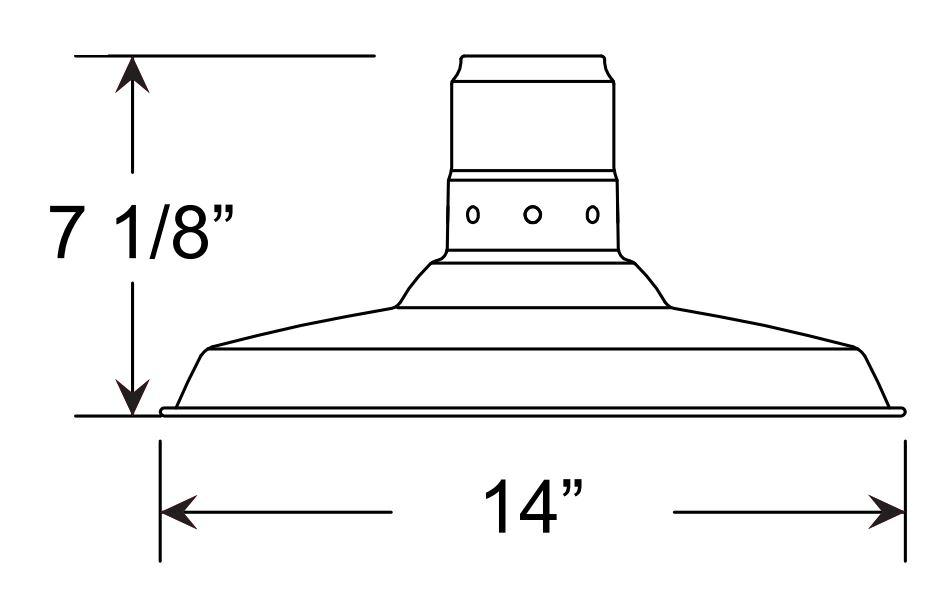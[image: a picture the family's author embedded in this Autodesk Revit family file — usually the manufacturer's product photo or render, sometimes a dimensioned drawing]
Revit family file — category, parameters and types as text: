
# Revit family: Shallow Dome_LED
name_source: partatom
category: Lighting Fixtures
units: mm (PartAtom-declared; Revit-internal decimal feet)

## family parameters
Always vertical = Yes
Cut with Voids When Loaded = No
Light Source = Yes
OmniClass Number = 23.80.70.00
OmniClass Title = Lighting
Part Type = Normal
Room Calculation Point = No
Round Connector Dimension = Use Diameter
Shared = No
Work Plane-Based = No

## types (4) — shared parameters
Body Colour = Spun aluminium
Body Material = body
Bulb = Bulb
CRI = >90
Color Filter = 16777215
Construction Material = Heavy Duty spun aluminum.
Default Elevation = 0' - 0"
Description = 120-277 Voltage
Dimming = 1%
Dimming Lamp Color Temperature Shift = <None>
Efficiency = 97-125 lumens per watt
Inside body material = Inside body
Lamp = LED
Life = L70 50,000 hours
Load Classification = Lighting
Manufacturer = ANP Lighting
Photometric Web File = generic.ies
Power Factor = 1
Tilt Angle = 90.00°
URL = https://www.anplighting.com
Voltage = 277 V
Warranty = 5 year limited warranty

## per-type parameters (varying)
| type | Apparent Load | Fixture Diameter | Fixture Height | SD10 | SD12 | SD16 | SD20 | Wattage Comments | Weight |
| SD10 | 10 VA | 0' - 10" | 0' - 5" | Yes | No | No | No | 10W | 1.0 lb |
| SD12 | 16 VA | 1' - 0" | 0' - 6" | No | Yes | No | No | 16W | 2.0 lb |
| SD16 | 24 VA | 1' - 4" | 0' - 8" | No | No | Yes | No | 24W | 3.0 lb |
| SD20 | 24 VA | 1' - 8" | 0' - 10" | No | No | No | Yes | 24W | 5.0 lb |

note: column(s) folded — value = type name in every type: Model

## geometry (parser evidence)
native form markers: Sweep x38
no freeform markers — native parametric forms only
